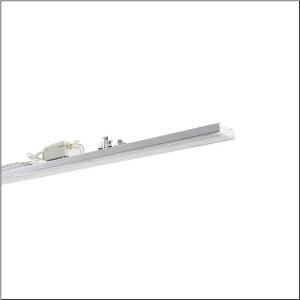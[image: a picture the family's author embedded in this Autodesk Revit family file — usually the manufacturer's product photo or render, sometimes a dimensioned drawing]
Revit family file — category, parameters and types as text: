
# Revit family: licross_11_recessed_mo_51tl10de445g
name_source: partatom
category: Lighting Fixtures
units: mm (PartAtom-declared; Revit-internal decimal feet)

## family parameters
Cut with Voids When Loaded = No
Host = Face
Light Source = No
Part Type = Normal
Room Calculation Point = No
Round Connector Dimension = Use Diameter
Shared = No

## types (1)
- --- (1 x LED, 4980 lm, 29.6 W, 4000K)
    Apparent Load = 30 VA
    CIE Flux Codes = 50 81 96 100 100
    Color Rendering = 80
    Color Temperature = 4000K
    Default Elevation = 1800 mm
    Description = Licross 11 Recessed MO, luminaire insert, of sheet steel, coil coated, white, length: 750mm, width: 66mm, height: 67mm, LED rated luminous flux: 4.980lm, light colour: 840, SDCM (Standard Deviation of Colour Matching)MacAdam ≤ 2 SDCM (initial), control gear: DALI 2, with plug, 5-pole, with phase selection, mains connection: 220..240V, AC, 50/60Hz, rated input power: 30W, internal wiring halogen-free, primary optical cover: cover, of PMMA, light emission: direct distribution, primary light characteristic: symmetric, protection rating (complete): IP40, insulation class (complete): insulation class I (protective earthing), certification: CE, ENEC, VDE, UKCA, protection symbol: D if used in an environment without relevant dust loads with corresponding accessories, impact resistance: IK06, permissible ambient temperature for indoor applications: -25..+35°C, corresponds to IFS (International Featured Standards) requirements for safety and quality in the food industry, reducing of maximum allowable ambient temperature of 5°C with ceiling mounting, LABS conformity tested according to VDMA 24364:2018-05, The light source and the operating device comply with the requirements of the Ecodesign Regulation (EU) 2019/2020 and are replaceable in accordance with this regulation, packaging unit: 1 piece
    Height = 58 mm
    Lamp = 1 x LED
    Lamp Light Flux = 4980 lm
    Lamp Power = 29.6 W
    Lamp count = 1
    Length = 750 mm
    Luminous efficacy = 168 lm/W
    Manufacturer = Siteco
    ModVariant = No
    Model = 51TL10DE445G
    Mounting Place = Ceiling
    Mounting Type = Pendant
    Number of Poles = 1
    OnlyDefault = Yes
    Power Factor = 1
    Product Name = Licross 11 Recessed MO
    Product group = luminaire insert | ceiling pendant
    ProductGroupID = 901
    Protection Class = Protection class I
    Protection Degree = IP 40
    RLX_Detail_Level = 1
    RLX_Emergency_Light_Flux = 0 lm
    RLX_Emergency_Type = 0
    RLX_Emergency_Type_DB = No
    RlxData = <blob elided: 29173 chars, md5=887124da>
    Socket = socket
    Standby Power = 0 W
    System Light Flux = 4980 lm
    System Power = 30 W
    Type Comments = factory setting: luminous flux: 100 % | dim-lin: 254 | 378 mA
    Type Image = l_1296930.jpg
    URL = http://relux.com
    VarID = @adj_102829
    Voltage = 0 V
    Weight = 0.00 kg
    Width = 66 mm

## geometry (parser evidence)
native form markers: Blend x4, Sweep x8
no freeform markers — native parametric forms only
